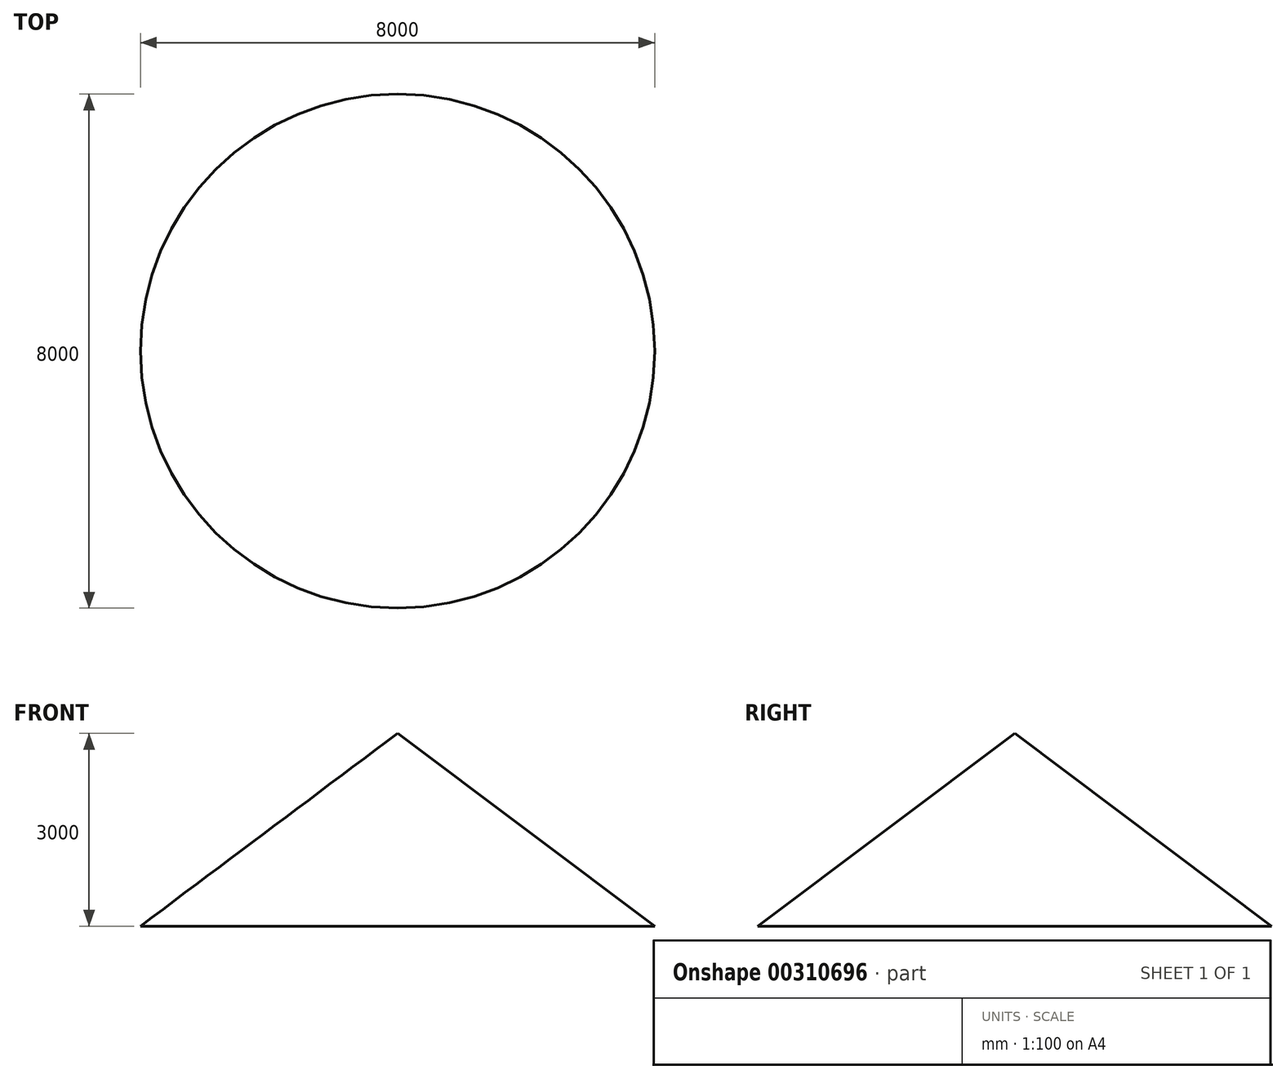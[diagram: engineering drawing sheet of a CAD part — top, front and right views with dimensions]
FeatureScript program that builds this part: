
annotation { "Feature Type Name" : "Feature", "Feature Type Description" : "" }
export const myFeature = defineFeature(function(context is Context, id is Id, definition is map)
    precondition{}
    {
        {
            var Q0;
            Q0=qCreatedBy(makeId("Front.planeOp"),FACE);
            var sketch = newSketch(context, id + "F0", { "sketchPlane" : qUnion([Q0])});
            skLineSegment(sketch, "E0", {"start": v(0, 0) * mm, "end": v(4000, 0) * mm});
            skLineSegment(sketch, "E1", {"start": v(4000, 0) * mm, "end": v(0, 3000) * mm});
            skLineSegment(sketch, "E2", {"start": v(0, 3000) * mm, "end": v(0, 0) * mm});
            skLineSegment(sketch, "E3", {"start": v(0, 3800.82) * mm, "end": v(0, -1363.27) * mm});
            skSolve(sketch);
        }
        {
            var Q0;
            {var subQ0=sQuery(id+"F0.wireOp",EDGE,"E0");Q0=makeQuery(id+"F0.imprint","IMPRINT",FACE,{"disambiguationData":[TD([[makeQuery(id+"F0.imprint","IMPRINT",EDGE,{"derivedFrom":subQ0}),1.0]])]});}
            var Q1;
            Q1=sQuery(id+"F0.wireOp",EDGE,"E3");
            revolve(context, id + "F1", {"entities" : qUnion([Q0]), "axis" : qUnion([Q1]), "revolveType" : RevolveType.FULL});
        }
    });
